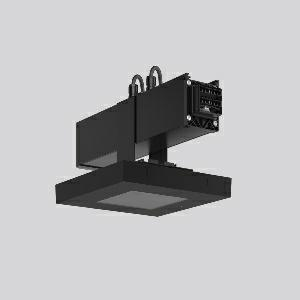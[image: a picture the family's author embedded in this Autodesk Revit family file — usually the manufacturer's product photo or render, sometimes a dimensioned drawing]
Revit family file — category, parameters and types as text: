
# Revit family: linedo_module_rw_9503rw_763_409_000_436b
name_source: partatom
category: Lighting Fixtures
units: mm (PartAtom-declared; Revit-internal decimal feet)

## family parameters
Cut with Voids When Loaded = No
Host = Face
Light Source = No
Part Type = Normal
Room Calculation Point = No
Round Connector Dimension = Use Diameter
Shared = No

## types (1)
- LINEDO Module RW (1 x LED Modul 765, 360 lm, 6500)
    Apparent Load = 7 VA
    CIE Flux Codes = 38 71 99 100 100
    Color Rendering = 70
    Color Temperature = 6500
    Default Elevation = 1800 mm
    Description = LINEDO, 6,7 W, 360 lm, 765, black, on/off
Continuous line luminaire, L 330 B 198 H 170, CBS, emergency-360 lm, AC-Control
    Height = 170 mm  [stored 0.557743 ft]
    Lamp = 1 x LED Modul 765
    Lamp Light Flux = 360 lm
    Lamp count = 1
    Length = 330 mm
    Lifetime = 50000 h
    Luminous efficacy = 54 lm/W
    Manufacturer = RZB
    ModVariant = No
    Model = 9503RW.763.409.000
    Mounting Place = Ceiling
    Mounting Type = Surface mounted, Pendant
    Number of Poles = 1
    OnlyDefault = Yes
    Power Factor = 1
    Product Name = LINEDO Module RW
    Product group = Surface mounted continuous line luminaire system
    ProductGroupID = 310
    Protection Class = Protection class I
    Protection Degree = IP 54
    RLX_Detail_Level = 1
    RLX_Emergency_Light_Flux = 360 lm
    RLX_Emergency_Type = 3
    RLX_Emergency_Type_DB = Yes
    RlxData = <blob elided: 34505 chars, md5=8a88909a>
    Socket = socket
    Standby Power = 0 W
    System Light Flux = 360 lm
    System Power = 7 W
    Type Comments = Product without accessories
    Type Image = 9503rw.763.434.000.jpg
    URL = http://relux.com
    VarID = ---
    Voltage = 230 V
    Voltage Range = 220-240 V
    Weight = 0.00 kg
    Width = 198 mm

note: [stored X ft] marks values corroborated as IEEE doubles in the binary element streams (Revit-internal decimal feet)

## geometry (parser evidence)
native form markers: Blend x4, Sweep x12
no freeform markers — native parametric forms only
